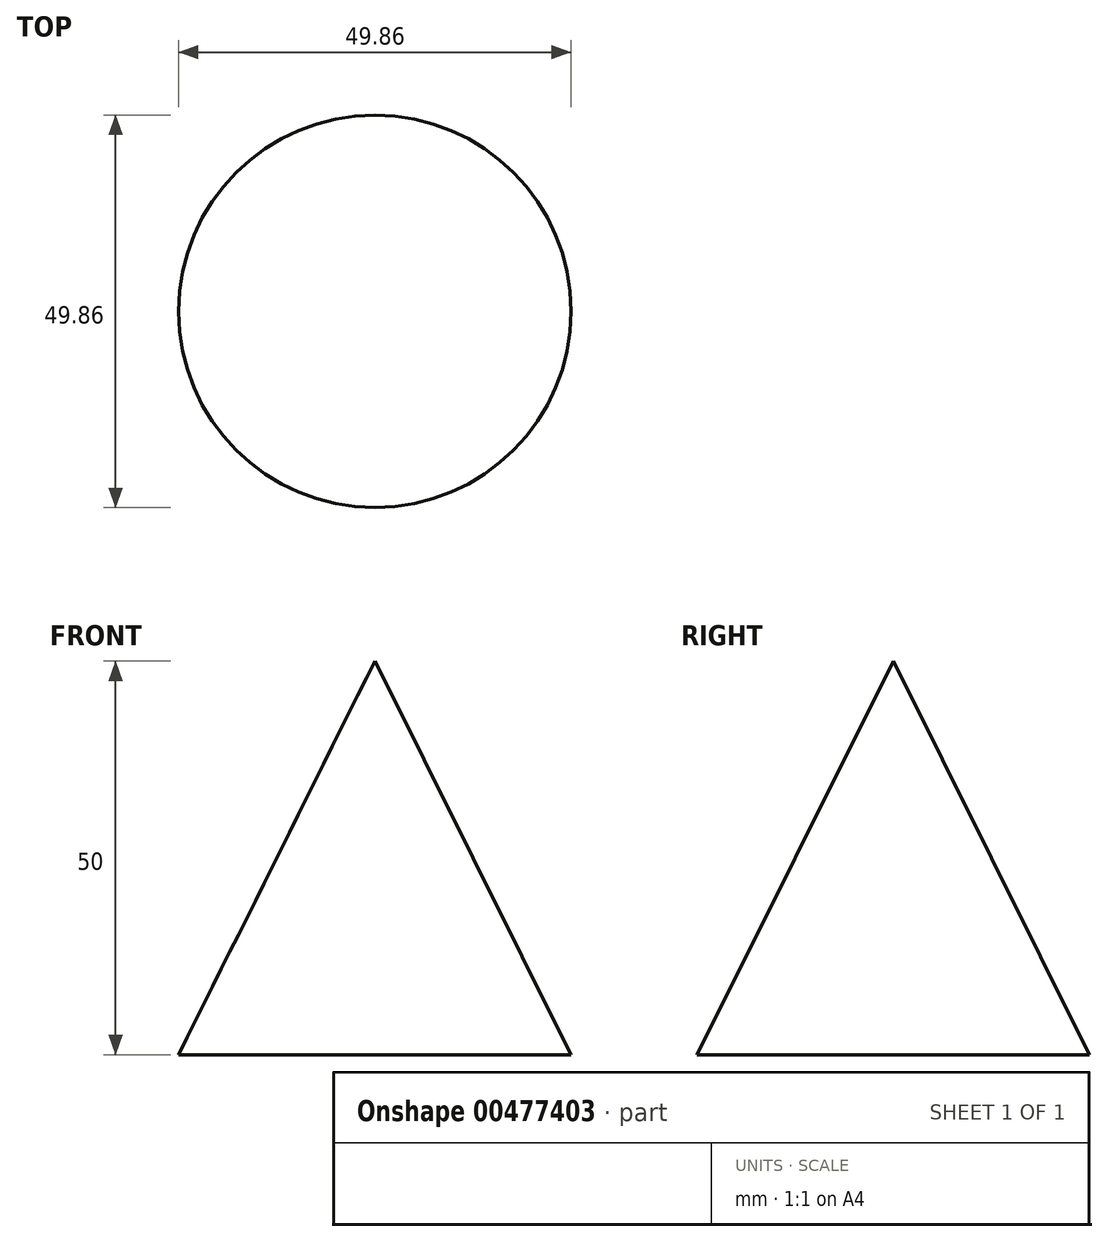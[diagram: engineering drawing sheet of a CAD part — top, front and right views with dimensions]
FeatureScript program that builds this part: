
annotation { "Feature Type Name" : "Feature", "Feature Type Description" : "" }
export const myFeature = defineFeature(function(context is Context, id is Id, definition is map)
    precondition{}
    {
        {
            var Q0;
            Q0=qCreatedBy(makeId("Top.planeOp"),FACE);
            var sketch = newSketch(context, id + "F0", { "sketchPlane" : qUnion([Q0])});
            skCircle(sketch, "E0", {"center": v(0, 0) * mm, "radius": 25 * mm});
            skSolve(sketch);
        }
        {
            var Q0;
            Q0=makeQuery(id+"F0.imprint","IMPRINT",FACE,{"disambiguationData":[TD([[makeQuery(id+"F0.imprint","IMPRINT",EDGE,{"derivedFrom":sQuery(id+"F0.wireOp",EDGE,"E0")}),1.0]])]});
            extrude(context, id + "F1", {"entities" : qUnion([Q0]), "depth" : 50 * mm, "offsetDistance" : 25 * mm});
        }
        {
            var Q0;
            Q0=makeQuery(id+"F1.opExtrude","CAP_FACE",FACE,{"disambiguationData":[OSD([sQuery(id+"F0.wireOp",EDGE,"E0")])],"isStart":false});
            chamfer(context, id + "F2", {"entities" : qUnion([Q0]), "chamferType" : ChamferType.OFFSET_ANGLE, "width" : 25 * mm, "oppositeDirection" : false, "angle" : 63.5 * degree, "tangentPropagation" : true});
        }
    });
